# Revit family: QF_ELECTROLUXPROFESSIONAL_1LSNJZ_IC64832FLF_G
name_source: partatom
category: Attrezzature speciali
units: mm (PartAtom-declared; Revit-internal decimal feet)

## family parameters
Basato su piano di lavoro = No
Condiviso = No
Punto di calcolo locali = No
Quota connettore circolare = Usa diametro
Sempre verticale = Sì
Taglio con vuoti quando caricato = No
Tipo di parte = Normale

## types (5) — shared parameters
Depth Actual = 1320 mm
Gas KW = 65
Height Actual = 1460 mm  [stored 4.79003 ft]
Latent Heat Output = 0.0
Length Actual = 3835 mm
Modello = IC64832FLF
Phase = 3
Produttore = Electrolux Professional
Sensible Heat Output = 0.0
URL = www.electroluxprofessional.com
Weight = 1330
zero-valued in all types: Prospetto di default, Steam Pounds per Hour

## per-type parameters (varying)
| type | Cycle | Descrizione | Item Number | Volts | Watts |
| 9882030019 | 50 Hz | IRONER CYLINDER IC64832FLF FEEDING+LENGTH FOLDING 3170MM SUPERIOR GAS CE 400/50/3 DUBIXIUM FR VAC.FEED.TABLE ANTISTATIC | 1LA06P | 415 V | 1750 W |
| 9882030028 | 50 Hz | IRONER CYLINDER IC64832FLF FEEDING+LENGTH FOLDING 3170MM SUPERIOR GAS CE 400/50/3 DUBIXIUM ML VAC.FEED.TABLE ANTISTATIC | 1LA094 | 400 V | 1750 W |
| 9882030291 | 60 Hz | IRONER CYLINDER IC64832FLF FEEDING+LENGTH FOLDING 3170MM SUPERIOR GAS USA 208-240/60/3 DUBIXIUM US-ES-FR VAC.FEED.TABLE | 1LM0BF | 240 V | 2000 W |
| 9882030146 | 60 Hz | IRONER CYLINDER IC64832FLF FEEDING+LENGTH FOLDING 3170MM SUPERIOR GAS CE 400/60/3 DUBIXIUM ML VAC.FEED.TABLE ANTISTATIC | 1L0HE9 | 400 V | 1750 W |
| 9882030181 | 60 Hz | IRONER CYLINDER IC64832FLF FEEDING+LENGTH FOLDING 3170MM SUPERIOR GAS CE 208-240/60/3 DUBIXIUM EN, ES, PO VAC.FEED.TABLE | 1L0GRU | 240 V | 2000 W |

note: [stored X ft] marks values corroborated as IEEE doubles in the binary element streams (Revit-internal decimal feet)

## geometry (parser evidence)
native form markers: Sweep x12
no freeform markers — native parametric forms only
